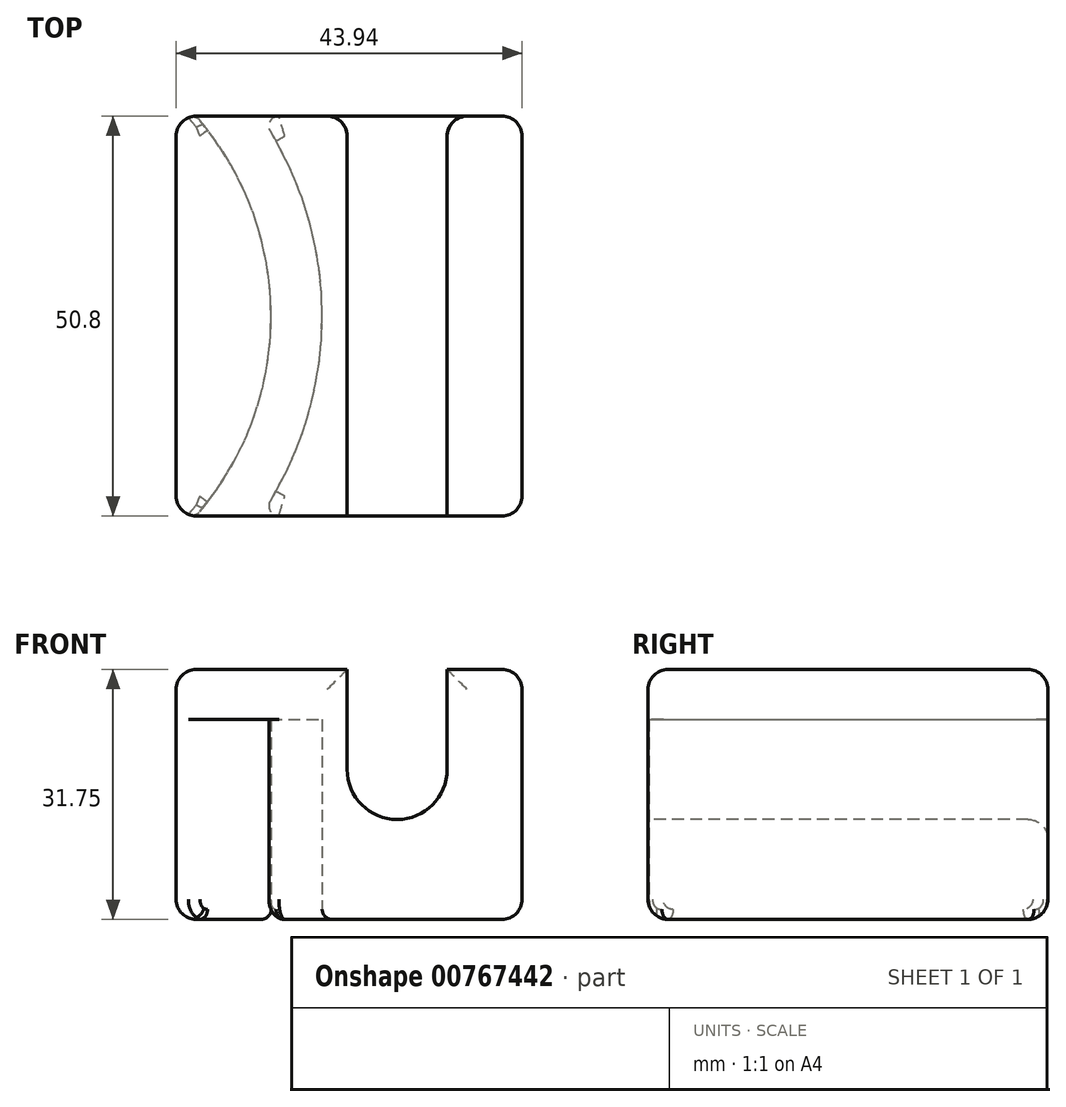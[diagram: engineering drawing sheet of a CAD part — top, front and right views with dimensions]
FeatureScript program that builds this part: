
annotation { "Feature Type Name" : "Feature", "Feature Type Description" : "" }
export const myFeature = defineFeature(function(context is Context, id is Id, definition is map)
    precondition{}
    {
        {
            var Q0;
            Q0=qCreatedBy(makeId("Top.planeOp"),FACE);
            var sketch = newSketch(context, id + "F0", { "sketchPlane" : qUnion([Q0])});
            skLineSegment(sketch, "E0.bottom", {"start": v(-21.97, 25.4) * mm, "end": v(21.97, 25.4) * mm});
            skLineSegment(sketch, "E0.top", {"start": v(-21.97, -25.4) * mm, "end": v(21.97, -25.4) * mm});
            skLineSegment(sketch, "E0.left", {"start": v(-21.97, 25.4) * mm, "end": v(-21.97, -25.4) * mm});
            skLineSegment(sketch, "E0.right", {"start": v(21.97, 25.4) * mm, "end": v(21.97, -25.4) * mm});
            skLineSegment(sketch, "E1", {"start": v(-21.97, 25.4) * mm, "end": v(0, 0) * mm, "construction": true});
            skLineSegment(sketch, "E2", {"start": v(0, 0) * mm, "end": v(21.97, -25.4) * mm, "construction": true});
            skArc(sketch, "E3", {"start": v(-19.43, -25.4) * mm, "mid": v(-9.9, 0) * mm, "end": v(-19.43, 25.4) * mm});
            skArc(sketch, "E4", {"start": v(-11.26, -25.4) * mm, "mid": v(-3.43, 0) * mm, "end": v(-11.26, 25.4) * mm});
            skLineSegment(sketch, "E5", {"start": v(-19.43, -25.4) * mm, "end": v(-19.43, 25.4) * mm, "construction": true});
            skSolve(sketch);
        }
        {
            var Q0;
            {var subQ0=sQuery(id+"F0.wireOp",EDGE,"E0.left");Q0=makeQuery(id+"F0.imprint","IMPRINT",FACE,{"disambiguationData":[TD([[makeQuery(id+"F0.imprint","IMPRINT",EDGE,{"derivedFrom":subQ0}),1.0]])]});}
            var Q1;
            {var subQ0=sQuery(id+"F0.wireOp",EDGE,"E0.right");Q1=makeQuery(id+"F0.imprint","IMPRINT",FACE,{"disambiguationData":[TD([[makeQuery(id+"F0.imprint","IMPRINT",EDGE,{"derivedFrom":subQ0}),-1.0]])]});}
            extrude(context, id + "F1", {"entities" : qUnion([Q0, Q1]), "depth" : 25.4 * mm, "offsetDistance" : 25.4 * mm});
        }
        {
            var Q0;
            Q0=makeQuery(id+"F1.opExtrude","CAP_FACE",FACE,{"disambiguationData":[OSD([sQuery(id+"F0.wireOp",EDGE,"E0.bottom"),sQuery(id+"F0.wireOp",EDGE,"E0.top"),sQuery(id+"F0.wireOp",EDGE,"E0.left"),sQuery(id+"F0.wireOp",EDGE,"E3")])],"isStart":false});
            var sketch = newSketch(context, id + "F2", { "sketchPlane" : qUnion([Q0])});
            skLineSegment(sketch, "E6.bottom", {"start": v(-21.97, 25.4) * mm, "end": v(21.97, 25.4) * mm});
            skLineSegment(sketch, "E6.top", {"start": v(-21.97, -25.4) * mm, "end": v(21.97, -25.4) * mm});
            skLineSegment(sketch, "E6.left", {"start": v(-21.97, 25.4) * mm, "end": v(-21.97, -25.4) * mm});
            skLineSegment(sketch, "E6.right", {"start": v(21.97, 25.4) * mm, "end": v(21.97, -25.4) * mm});
            skSolve(sketch);
        }
        {
            var Q0;
            Q0 = qSketchRegion(id + "F2", true);
            extrude(context, id + "F3", {"entities" : qUnion([Q0]), "operationType" : NewBodyOperationType.ADD, "depth" : 6.35 * mm, "offsetDistance" : 25.4 * mm});
        }
        {
            var Q0;
            {var subQ0=sQuery(id+"F0.wireOp",EDGE,"E0.top");Q0=makeQuery(id+"F3.boolean.opBoolean","MERGE",FACE,{"derivedFrom":[makeQuery(id+"F1.opExtrude","SWEPT_FACE",FACE,{"disambiguationData":[OSD([subQ0]),TDD([makeQuery(id+"F0.imprint","IMPRINT",EDGE,{"disambiguationData":[TD([[makeQuery(id+"F0.imprint","INTERSECT",VERTEX,{"derivedFrom":[subQ0,sQuery(id+"F0.wireOp",EDGE,"E0.left")]}),-1.0]])],"derivedFrom":subQ0})])]}),makeQuery(id+"F1.opExtrude","SWEPT_FACE",FACE,{"disambiguationData":[OSD([subQ0]),TDD([makeQuery(id+"F0.imprint","IMPRINT",EDGE,{"disambiguationData":[TD([[makeQuery(id+"F0.imprint","INTERSECT",VERTEX,{"derivedFrom":[subQ0,sQuery(id+"F0.wireOp",EDGE,"E0.right")]}),1.0]])],"derivedFrom":subQ0})])]}),makeQuery(id+"F3.opExtrude","SWEPT_FACE",FACE,{"disambiguationData":[OSD([sQuery(id+"F2.wireOp",EDGE,"E6.top")])]})]});}
            var sketch = newSketch(context, id + "F4", { "sketchPlane" : qUnion([Q0])});
            skLineSegment(sketch, "E7.bottom", {"start": v(-0.25, 31.75) * mm, "end": v(12.45, 31.75) * mm});
            skLineSegment(sketch, "E7.top", {"start": v(-0.25, 19.05) * mm, "end": v(12.45, 19.05) * mm});
            skLineSegment(sketch, "E7.left", {"start": v(-0.25, 31.75) * mm, "end": v(-0.25, 19.05) * mm});
            skLineSegment(sketch, "E7.right", {"start": v(12.45, 31.75) * mm, "end": v(12.45, 19.05) * mm});
            skArc(sketch, "E8", {"start": v(-0.25, 19.05) * mm, "mid": v(6.1, 12.7) * mm, "end": v(12.45, 19.05) * mm});
            skPoint(sketch, "E8.midSnap0", {"position": v(6.1, 19.05) * mm});
            skSolve(sketch);
        }
        {
            var Q0;
            Q0 = qSketchRegion(id + "F4", true);
            extrude(context, id + "F5", {"entities" : qUnion([Q0]), "operationType" : NewBodyOperationType.REMOVE, "endBound" : BoundingType.THROUGH_ALL, "oppositeDirection" : true, "depth" : 25.4 * mm, "offsetDistance" : 25.4 * mm});
        }
        {
            var Q0;
            Q0=makeQuery(id+"F3.opExtrude","CAP_EDGE",EDGE,{"disambiguationData":[OSD([sQuery(id+"F2.wireOp",EDGE,"E6.right")])],"isStart":false});
            var Q1;
            Q1=makeQuery(id+"F1.opExtrude","CAP_EDGE",EDGE,{"disambiguationData":[OSD([sQuery(id+"F0.wireOp",EDGE,"E0.right")])],"isStart":true});
            var Q2;
            Q2=makeQuery(id+"F3.opExtrude","CAP_EDGE",EDGE,{"disambiguationData":[OSD([sQuery(id+"F2.wireOp",EDGE,"E6.left")])],"isStart":false});
            var Q3;
            {var subQ0=sQuery(id+"F0.wireOp",EDGE,"E0.top");Q3=makeQuery(id+"F1.opExtrude","CAP_EDGE",EDGE,{"disambiguationData":[OSD([subQ0]),TDD([makeQuery(id+"F0.imprint","IMPRINT",EDGE,{"disambiguationData":[TD([[makeQuery(id+"F0.imprint","INTERSECT",VERTEX,{"derivedFrom":[subQ0,sQuery(id+"F0.wireOp",EDGE,"E0.right")]}),1.0]])],"derivedFrom":subQ0})])],"isStart":true});}
            var Q4;
            {var subQ0=sQuery(id+"F0.wireOp",EDGE,"E0.bottom");Q4=makeQuery(id+"F1.opExtrude","CAP_EDGE",EDGE,{"disambiguationData":[OSD([subQ0]),TDD([makeQuery(id+"F0.imprint","IMPRINT",EDGE,{"disambiguationData":[TD([[makeQuery(id+"F0.imprint","INTERSECT",VERTEX,{"derivedFrom":[subQ0,sQuery(id+"F0.wireOp",EDGE,"E0.right")]}),1.0]])],"derivedFrom":subQ0})])],"isStart":true});}
            var Q5;
            Q5=makeQuery(id+"F3.boolean.opBoolean","MERGE",EDGE,{"derivedFrom":[makeQuery(id+"F1.opExtrude","SWEPT_EDGE",EDGE,{"disambiguationData":[OSD([sQuery(id+"F0.wireOp",EDGE,"E0.top"),sQuery(id+"F0.wireOp",EDGE,"E0.right")])]}),makeQuery(id+"F3.opExtrude","SWEPT_EDGE",EDGE,{"disambiguationData":[OSD([sQuery(id+"F2.wireOp",EDGE,"E6.top"),sQuery(id+"F2.wireOp",EDGE,"E6.right")])]})]});
            var Q6;
            Q6=makeQuery(id+"F3.boolean.opBoolean","MERGE",EDGE,{"derivedFrom":[makeQuery(id+"F1.opExtrude","SWEPT_EDGE",EDGE,{"disambiguationData":[OSD([sQuery(id+"F0.wireOp",EDGE,"E0.bottom"),sQuery(id+"F0.wireOp",EDGE,"E0.right")])]}),makeQuery(id+"F3.opExtrude","SWEPT_EDGE",EDGE,{"disambiguationData":[OSD([sQuery(id+"F2.wireOp",EDGE,"E6.bottom"),sQuery(id+"F2.wireOp",EDGE,"E6.right")])]})]});
            var Q7;
            {var subQ1=sQuery(id+"F2.wireOp",EDGE,"E6.top");var subQ2=sQuery(id+"F0.wireOp",EDGE,"E0.left");Q7=makeQuery(id+"F5.boolean.opBoolean","SPLIT",EDGE,{"disambiguationData":[TD([makeQuery(id+"F1.opExtrude","SWEPT_FACE",FACE,{"disambiguationData":[OSD([subQ2])]})])],"derivedFrom":makeQuery(id+"F3.opExtrude","CAP_EDGE",EDGE,{"disambiguationData":[OSD([subQ1])],"isStart":false})});}
            var Q8;
            {var subQ0=sQuery(id+"F2.wireOp",EDGE,"E6.bottom");var subQ1=sQuery(id+"F0.wireOp",EDGE,"E0.left");Q8=makeQuery(id+"F5.boolean.opBoolean","SPLIT",EDGE,{"disambiguationData":[TD([makeQuery(id+"F1.opExtrude","SWEPT_FACE",FACE,{"disambiguationData":[OSD([subQ1])]})])],"derivedFrom":makeQuery(id+"F3.opExtrude","CAP_EDGE",EDGE,{"disambiguationData":[OSD([subQ0])],"isStart":false})});}
            var Q9;
            {var subQ1=sQuery(id+"F2.wireOp",EDGE,"E6.top");var subQ2=sQuery(id+"F0.wireOp",EDGE,"E0.right");Q9=makeQuery(id+"F5.boolean.opBoolean","SPLIT",EDGE,{"disambiguationData":[TD([makeQuery(id+"F1.opExtrude","SWEPT_FACE",FACE,{"disambiguationData":[OSD([subQ2])]})])],"derivedFrom":makeQuery(id+"F3.opExtrude","CAP_EDGE",EDGE,{"disambiguationData":[OSD([subQ1])],"isStart":false})});}
            var Q10;
            {var subQ0=sQuery(id+"F0.wireOp",EDGE,"E0.right");var subQ1=sQuery(id+"F2.wireOp",EDGE,"E6.bottom");Q10=makeQuery(id+"F5.boolean.opBoolean","SPLIT",EDGE,{"disambiguationData":[TD([makeQuery(id+"F1.opExtrude","SWEPT_FACE",FACE,{"disambiguationData":[OSD([subQ0])]})])],"derivedFrom":makeQuery(id+"F3.opExtrude","CAP_EDGE",EDGE,{"disambiguationData":[OSD([subQ1])],"isStart":false})});}
            var Q11;
            Q11=makeQuery(id+"F5.boolean.opBoolean","COPY",EDGE,{"derivedFrom":makeQuery(id+"F5.opExtrude","CAP_EDGE",EDGE,{"disambiguationData":[OSD([sQuery(id+"F4.wireOp",EDGE,"E8")])],"isStart":true})});
            var Q12;
            {var subQ0=sQuery(id+"F0.wireOp",EDGE,"E0.bottom");Q12=makeQuery(id+"F5.boolean.opBoolean","INTERSECT",EDGE,{"derivedFrom":[makeQuery(id+"F3.boolean.opBoolean","MERGE",FACE,{"derivedFrom":[makeQuery(id+"F1.opExtrude","SWEPT_FACE",FACE,{"disambiguationData":[OSD([subQ0]),TDD([makeQuery(id+"F0.imprint","IMPRINT",EDGE,{"disambiguationData":[TD([[makeQuery(id+"F0.imprint","INTERSECT",VERTEX,{"derivedFrom":[subQ0,sQuery(id+"F0.wireOp",EDGE,"E0.left")]}),-1.0]])],"derivedFrom":subQ0})])]}),makeQuery(id+"F1.opExtrude","SWEPT_FACE",FACE,{"disambiguationData":[OSD([subQ0]),TDD([makeQuery(id+"F0.imprint","IMPRINT",EDGE,{"disambiguationData":[TD([[makeQuery(id+"F0.imprint","INTERSECT",VERTEX,{"derivedFrom":[subQ0,sQuery(id+"F0.wireOp",EDGE,"E0.right")]}),1.0]])],"derivedFrom":subQ0})])]}),makeQuery(id+"F3.opExtrude","SWEPT_FACE",FACE,{"disambiguationData":[OSD([sQuery(id+"F2.wireOp",EDGE,"E6.bottom")])]})]}),makeQuery(id+"F5.opExtrude","SWEPT_FACE",FACE,{"disambiguationData":[OSD([sQuery(id+"F4.wireOp",EDGE,"E8")])]})]});}
            var Q13;
            Q13=makeQuery(id+"F1.opExtrude","CAP_EDGE",EDGE,{"disambiguationData":[OSD([sQuery(id+"F0.wireOp",EDGE,"E0.left")])],"isStart":true});
            var Q14;
            Q14=makeQuery(id+"F3.boolean.opBoolean","MERGE",EDGE,{"derivedFrom":[makeQuery(id+"F1.opExtrude","SWEPT_EDGE",EDGE,{"disambiguationData":[OSD([sQuery(id+"F0.wireOp",EDGE,"E0.top"),sQuery(id+"F0.wireOp",EDGE,"E0.left")])]}),makeQuery(id+"F3.opExtrude","SWEPT_EDGE",EDGE,{"disambiguationData":[OSD([sQuery(id+"F2.wireOp",EDGE,"E6.top"),sQuery(id+"F2.wireOp",EDGE,"E6.left")])]})]});
            var Q15;
            {var subQ0=sQuery(id+"F0.wireOp",EDGE,"E0.top");Q15=makeQuery(id+"F1.opExtrude","CAP_EDGE",EDGE,{"disambiguationData":[OSD([subQ0]),TDD([makeQuery(id+"F0.imprint","IMPRINT",EDGE,{"disambiguationData":[TD([[makeQuery(id+"F0.imprint","INTERSECT",VERTEX,{"derivedFrom":[subQ0,sQuery(id+"F0.wireOp",EDGE,"E0.left")]}),-1.0]])],"derivedFrom":subQ0})])],"isStart":true});}
            var Q16;
            {var subQ0=sQuery(id+"F0.wireOp",EDGE,"E0.bottom");Q16=makeQuery(id+"F1.opExtrude","CAP_EDGE",EDGE,{"disambiguationData":[OSD([subQ0]),TDD([makeQuery(id+"F0.imprint","IMPRINT",EDGE,{"disambiguationData":[TD([[makeQuery(id+"F0.imprint","INTERSECT",VERTEX,{"derivedFrom":[subQ0,sQuery(id+"F0.wireOp",EDGE,"E0.left")]}),-1.0]])],"derivedFrom":subQ0})])],"isStart":true});}
            var Q17;
            Q17=makeQuery(id+"F3.boolean.opBoolean","MERGE",EDGE,{"derivedFrom":[makeQuery(id+"F1.opExtrude","SWEPT_EDGE",EDGE,{"disambiguationData":[OSD([sQuery(id+"F0.wireOp",EDGE,"E0.bottom"),sQuery(id+"F0.wireOp",EDGE,"E0.left")])]}),makeQuery(id+"F3.opExtrude","SWEPT_EDGE",EDGE,{"disambiguationData":[OSD([sQuery(id+"F2.wireOp",EDGE,"E6.bottom"),sQuery(id+"F2.wireOp",EDGE,"E6.left")])]})]});
            fillet(context, id + "F6", {"entities" : qUnion([Q0, Q1, Q2, Q3, Q4, Q5, Q6, Q7, Q8, Q9, Q10, Q11, Q12, Q13, Q14, Q15, Q16, Q17]), "radius" : 2.54 * mm, "tangentPropagation" : true, "allowEdgeOverflow" : false});
        }
        {
            var Q0;
            Q0=makeQuery(id+"F1.opExtrude","CAP_EDGE",EDGE,{"disambiguationData":[OSD([sQuery(id+"F0.wireOp",EDGE,"E3")])],"isStart":true});
            var Q1;
            Q1=makeQuery(id+"F5.boolean.opBoolean","COPY",EDGE,{"derivedFrom":makeQuery(id+"F5.opExtrude","SWEPT_EDGE",EDGE,{"disambiguationData":[OSD([sQuery(id+"F2.wireOp",EDGE,"E6.top"),sQuery(id+"F4.wireOp",EDGE,"E7.bottom"),sQuery(id+"F4.wireOp",EDGE,"E7.left")])]})});
            var Q2;
            Q2=makeQuery(id+"F5.boolean.opBoolean","COPY",EDGE,{"derivedFrom":makeQuery(id+"F5.opExtrude","SWEPT_EDGE",EDGE,{"disambiguationData":[OSD([sQuery(id+"F2.wireOp",EDGE,"E6.top"),sQuery(id+"F4.wireOp",EDGE,"E7.bottom"),sQuery(id+"F4.wireOp",EDGE,"E7.right")])]})});
            var Q3;
            {var subQ0=sQuery(id+"F0.wireOp",EDGE,"E0.bottom");Q3=makeQuery(id+"F5.boolean.opBoolean","INTERSECT",EDGE,{"derivedFrom":[makeQuery(id+"F3.boolean.opBoolean","MERGE",FACE,{"derivedFrom":[makeQuery(id+"F1.opExtrude","SWEPT_FACE",FACE,{"disambiguationData":[OSD([subQ0]),TDD([makeQuery(id+"F0.imprint","IMPRINT",EDGE,{"disambiguationData":[TD([[makeQuery(id+"F0.imprint","INTERSECT",VERTEX,{"derivedFrom":[subQ0,sQuery(id+"F0.wireOp",EDGE,"E0.left")]}),-1.0]])],"derivedFrom":subQ0})])]}),makeQuery(id+"F1.opExtrude","SWEPT_FACE",FACE,{"disambiguationData":[OSD([subQ0]),TDD([makeQuery(id+"F0.imprint","IMPRINT",EDGE,{"disambiguationData":[TD([[makeQuery(id+"F0.imprint","INTERSECT",VERTEX,{"derivedFrom":[subQ0,sQuery(id+"F0.wireOp",EDGE,"E0.right")]}),1.0]])],"derivedFrom":subQ0})])]}),makeQuery(id+"F3.opExtrude","SWEPT_FACE",FACE,{"disambiguationData":[OSD([sQuery(id+"F2.wireOp",EDGE,"E6.bottom")])]})]}),makeQuery(id+"F5.opExtrude","SWEPT_FACE",FACE,{"disambiguationData":[OSD([sQuery(id+"F4.wireOp",EDGE,"E7.right")])]})]});}
            var Q4;
            Q4=makeQuery(id+"F5.boolean.opBoolean","COPY",EDGE,{"derivedFrom":makeQuery(id+"F5.opExtrude","CAP_EDGE",EDGE,{"disambiguationData":[OSD([sQuery(id+"F4.wireOp",EDGE,"E7.left")])],"isStart":true})});
            var Q5;
            Q5=makeQuery(id+"F1.opExtrude","CAP_EDGE",EDGE,{"disambiguationData":[OSD([sQuery(id+"F0.wireOp",EDGE,"E4")])],"isStart":true});
            var Q6;
            Q6=makeQuery(id+"F1.opExtrude","SWEPT_EDGE",EDGE,{"disambiguationData":[OSD([sQuery(id+"F0.wireOp",EDGE,"E0.bottom"),sQuery(id+"F0.wireOp",EDGE,"E3")])]});
            var Q7;
            Q7=makeQuery(id+"F1.opExtrude","SWEPT_EDGE",EDGE,{"disambiguationData":[OSD([sQuery(id+"F0.wireOp",EDGE,"E0.top"),sQuery(id+"F0.wireOp",EDGE,"E3")])]});
            fillet(context, id + "F7", {"entities" : qUnion([Q0, Q1, Q2, Q3, Q4, Q5, Q6, Q7]), "radius" : 1.27 * mm, "tangentPropagation" : true, "allowEdgeOverflow" : false});
        }
    });
